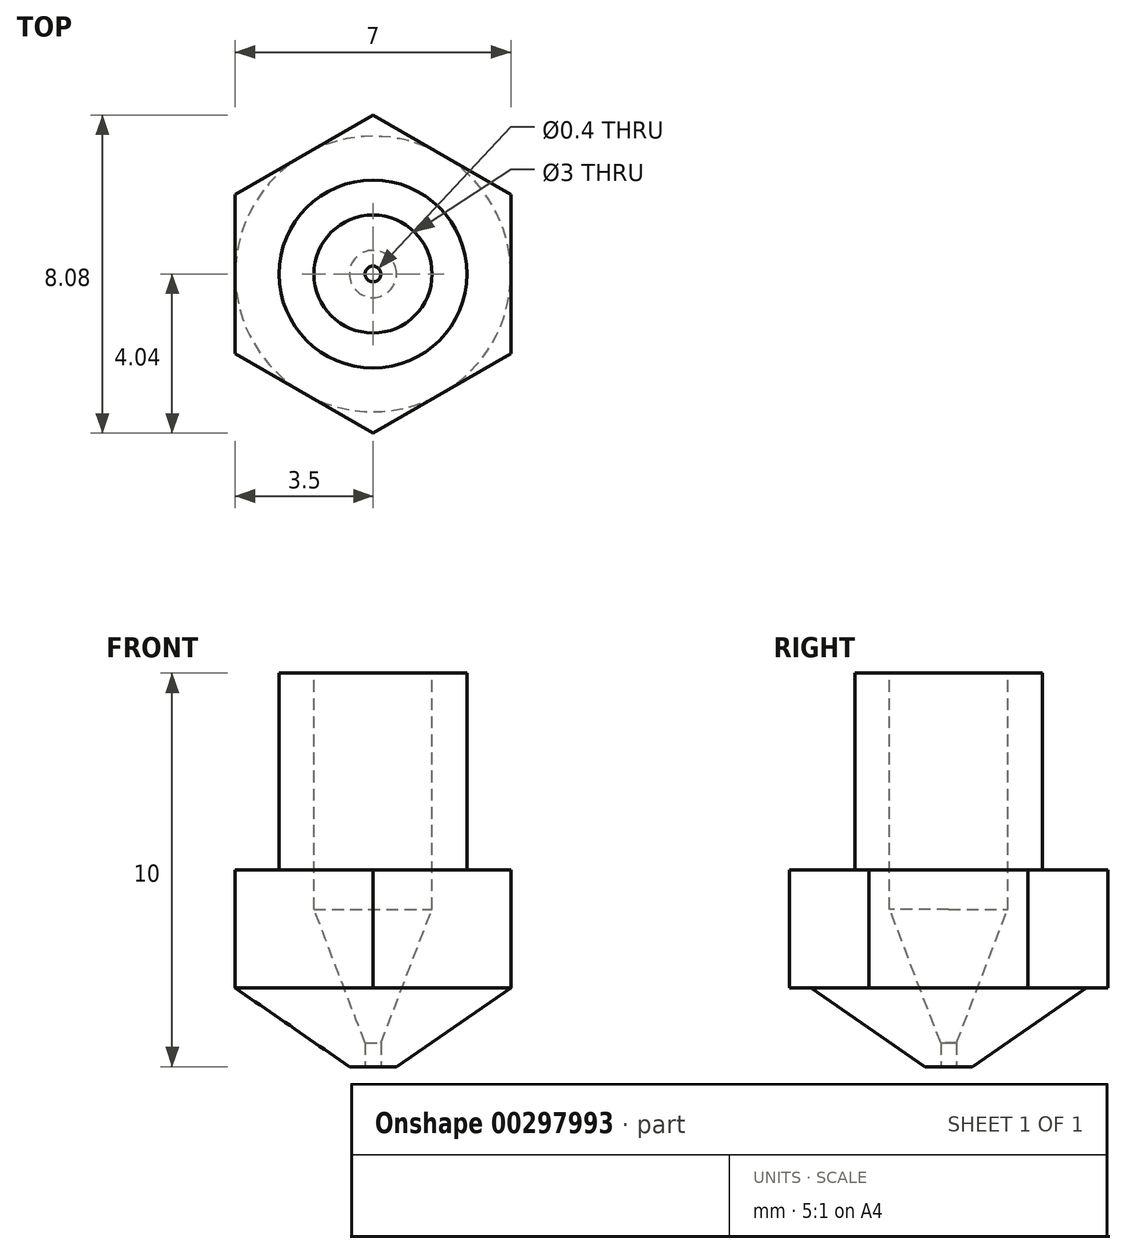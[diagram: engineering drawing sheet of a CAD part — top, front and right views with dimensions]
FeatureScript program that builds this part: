
annotation { "Feature Type Name" : "Feature", "Feature Type Description" : "" }
export const myFeature = defineFeature(function(context is Context, id is Id, definition is map)
    precondition{}
    {
        {
            var Q0;
            Q0=qCreatedBy(makeId("Top.planeOp"),FACE);
            cPlane(context, id + "F0", {"entities" : qUnion([Q0]), "cplaneType" : CPlaneType.OFFSET, "offset" : 2 * mm, "oppositeDirection" : true, "width" : 150 * mm, "height" : 150 * mm});
        }
        {
            var Q0;
            Q0=qCreatedBy(makeId("Top.planeOp"),FACE);
            var sketch = newSketch(context, id + "F1", { "sketchPlane" : qUnion([Q0])});
            skCircle(sketch, "E0.cCircle", {"center": v(0, 0) * mm, "radius": 3.5 * mm, "construction": true});
            skLineSegment(sketch, "E0.0", {"start": v(3.5, 2.02) * mm, "end": v(3.5, -2.02) * mm});
            skLineSegment(sketch, "E0.1", {"start": v(3.5, -2.02) * mm, "end": v(0, -4.04) * mm});
            skLineSegment(sketch, "E0.2", {"start": v(0, -4.04) * mm, "end": v(-3.5, -2.02) * mm});
            skLineSegment(sketch, "E0.3", {"start": v(-3.5, -2.02) * mm, "end": v(-3.5, 2.02) * mm});
            skLineSegment(sketch, "E0.4", {"start": v(-3.5, 2.02) * mm, "end": v(0, 4.04) * mm});
            skLineSegment(sketch, "E0.5", {"start": v(0, 4.04) * mm, "end": v(3.5, 2.02) * mm});
            skPoint(sketch, "E0.0.midPoint", {"position": v(3.5, 0) * mm});
            skSolve(sketch);
        }
        {
            var Q0;
            Q0=makeQuery(id+"F1.imprint","IMPRINT",FACE,{"disambiguationData":[TD([[makeQuery(id+"F1.imprint","IMPRINT",EDGE,{"derivedFrom":sQuery(id+"F1.wireOp",EDGE,"E0.0")}),-1.0]])]});
            extrude(context, id + "F2", {"entities" : qUnion([Q0]), "depth" : 3 * mm});
        }
        {
            var Q0;
            Q0=makeQuery(id+"F2.opExtrude","CAP_FACE",FACE,{"disambiguationData":[OSD([sQuery(id+"F1.wireOp",EDGE,"E0.0"),sQuery(id+"F1.wireOp",EDGE,"E0.1"),sQuery(id+"F1.wireOp",EDGE,"E0.2"),sQuery(id+"F1.wireOp",EDGE,"E0.3"),sQuery(id+"F1.wireOp",EDGE,"E0.4"),sQuery(id+"F1.wireOp",EDGE,"E0.5")])],"isStart":false});
            var sketch = newSketch(context, id + "F3", { "sketchPlane" : qUnion([Q0])});
            skCircle(sketch, "E1", {"center": v(0, 0) * mm, "radius": 2.39 * mm});
            skSolve(sketch);
        }
        {
            var Q0;
            Q0=makeQuery(id+"F3.imprint","IMPRINT",FACE,{"disambiguationData":[TD([[makeQuery(id+"F3.imprint","IMPRINT",EDGE,{"derivedFrom":sQuery(id+"F3.wireOp",EDGE,"E1")}),1.0]])]});
            extrude(context, id + "F4", {"entities" : qUnion([Q0]), "operationType" : NewBodyOperationType.ADD, "depth" : 5 * mm});
        }
        {
            var Q0;
            Q0=qCreatedBy(makeId("Front.planeOp"),FACE);
            var sketch = newSketch(context, id + "F5", { "sketchPlane" : qUnion([Q0])});
            skLineSegment(sketch, "E2", {"start": v(0, 0) * mm, "end": v(-3.5, 0) * mm});
            skLineSegment(sketch, "E3", {"start": v(0, -2) * mm, "end": v(0, 0) * mm});
            skPoint(sketch, "E4.orphan", {"position": v(3.5, 0) * mm});
            skLineSegment(sketch, "E5", {"start": v(-3.5, 0) * mm, "end": v(-0.6, -2) * mm});
            skLineSegment(sketch, "E6", {"start": v(-0.6, -2) * mm, "end": v(0, -2) * mm});
            skSolve(sketch);
        }
        {
            var Q0;
            Q0=makeQuery(id+"F5.imprint","IMPRINT",FACE,{"disambiguationData":[TD([[makeQuery(id+"F5.imprint","IMPRINT",EDGE,{"derivedFrom":sQuery(id+"F5.wireOp",EDGE,"E2")}),1.0]])]});
            var Q1;
            Q1=sQuery(id+"F5.wireOp",EDGE,"E3");
            revolve(context, id + "F6", {"operationType" : NewBodyOperationType.ADD, "entities" : qUnion([Q0]), "axis" : qUnion([Q1]), "revolveType" : RevolveType.FULL});
        }
        {
            var Q0;
            Q0=makeQuery(id+"F4.opExtrude","CAP_FACE",FACE,{"disambiguationData":[OSD([sQuery(id+"F3.wireOp",EDGE,"E1")])],"isStart":false});
            var sketch = newSketch(context, id + "F7", { "sketchPlane" : qUnion([Q0])});
            skPoint(sketch, "E7", {"position": v(0, 0) * mm});
            skSolve(sketch);
        }
        {
            var Q0;
            Q0=sQuery(id+"F7.wireOp",VERTEX,"E7");
            var Q1;
            Q1=makeQuery(id+"F2.opExtrude","SWEPT_BODY",BODY,{"disambiguationData":[OSD([sQuery(id+"F1.wireOp",EDGE,"E0.0"),sQuery(id+"F1.wireOp",EDGE,"E0.1"),sQuery(id+"F1.wireOp",EDGE,"E0.2"),sQuery(id+"F1.wireOp",EDGE,"E0.3"),sQuery(id+"F1.wireOp",EDGE,"E0.4"),sQuery(id+"F1.wireOp",EDGE,"E0.5")])]});
            hole(context, id + "F8", {"style" : HoleStyle.SIMPLE, "endStyle" : HoleEndStyle.BLIND, "holeDiameter" : 3 * mm, "holeDepth" : 6 * mm, "tappedDepth" : 12 * mm, "tapClearance" : 3, "locations" : qUnion([Q0]), "scope" : qUnion([Q1])});
        }
        {
            var Q0;
            Q0=qCreatedBy(id+"F0.planeOp",FACE);
            var sketch = newSketch(context, id + "F9", { "sketchPlane" : qUnion([Q0])});
            skPoint(sketch, "E8", {"position": v(0, 0) * mm});
            skSolve(sketch);
        }
        {
            var Q0;
            Q0=sQuery(id+"F9.wireOp",VERTEX,"E8");
            var Q1;
            Q1=makeQuery(id+"F2.opExtrude","SWEPT_BODY",BODY,{"disambiguationData":[OSD([sQuery(id+"F1.wireOp",EDGE,"E0.0"),sQuery(id+"F1.wireOp",EDGE,"E0.1"),sQuery(id+"F1.wireOp",EDGE,"E0.2"),sQuery(id+"F1.wireOp",EDGE,"E0.3"),sQuery(id+"F1.wireOp",EDGE,"E0.4"),sQuery(id+"F1.wireOp",EDGE,"E0.5")])]});
            hole(context, id + "F10", {"style" : HoleStyle.SIMPLE, "endStyle" : HoleEndStyle.BLIND, "oppositeDirection" : true, "holeDiameter" : 0.4 * mm, "holeDepth" : 6 * mm, "tappedDepth" : 12 * mm, "tapClearance" : 3, "locations" : qUnion([Q0]), "scope" : qUnion([Q1])});
        }
        {
            var Q0;
            Q0=qCreatedBy(makeId("Front.planeOp"),FACE);
            var sketch = newSketch(context, id + "F11", { "sketchPlane" : qUnion([Q0])});
            skPoint(sketch, "E9.0", {"position": v(0, 0) * mm});
            skLineSegment(sketch, "E10", {"start": v(3.5, 0) * mm, "end": v(0.6, -2) * mm});
            skLineSegment(sketch, "E11", {"start": v(-0.6, -2) * mm, "end": v(-3.5, 0) * mm});
            skLineSegment(sketch, "E12.0", {"start": v(-1.5, 2) * mm, "end": v(0, 2) * mm});
            skLineSegment(sketch, "E13", {"start": v(-1.5, 2) * mm, "end": v(-0.2, -1.4) * mm});
            skLineSegment(sketch, "E14", {"start": v(-0.2, -1.4) * mm, "end": v(0, -1.4) * mm});
            skLineSegment(sketch, "E15", {"start": v(0, 2) * mm, "end": v(0, -1.4) * mm});
            skSolve(sketch);
        }
        {
            var Q0;
            Q0=makeQuery(id+"F11.imprint","IMPRINT",FACE,{"disambiguationData":[TD([[makeQuery(id+"F11.imprint","IMPRINT",EDGE,{"derivedFrom":sQuery(id+"F11.wireOp",EDGE,"E12.0")}),-1.0]])]});
            var Q1;
            Q1=sQuery(id+"F11.wireOp",EDGE,"E15");
            revolve(context, id + "F12", {"operationType" : NewBodyOperationType.REMOVE, "entities" : qUnion([Q0]), "axis" : qUnion([Q1]), "revolveType" : RevolveType.FULL, "oppositeDirection" : true});
        }
    });
